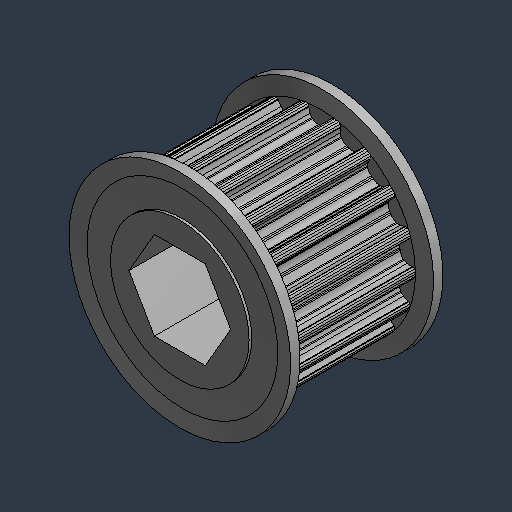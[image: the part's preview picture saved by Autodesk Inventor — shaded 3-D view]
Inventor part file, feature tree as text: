
AUTODESK INVENTOR PART (.ipt)
format: ipt  version: 2024.3 (Build 283343000, 343)  size: 437,248 bytes
history: native  units: mm (DEFAULTED — no unit token found)
features: mirror x1
ambient origin geometry x8: Origin, YZ Plane, XZ Plane, XY Plane, X Axis, Y Axis, Z Axis, Center Point
bodies: Solid1 (feature_tree)
feature tree (1):
  mirror  "Mirror1"
